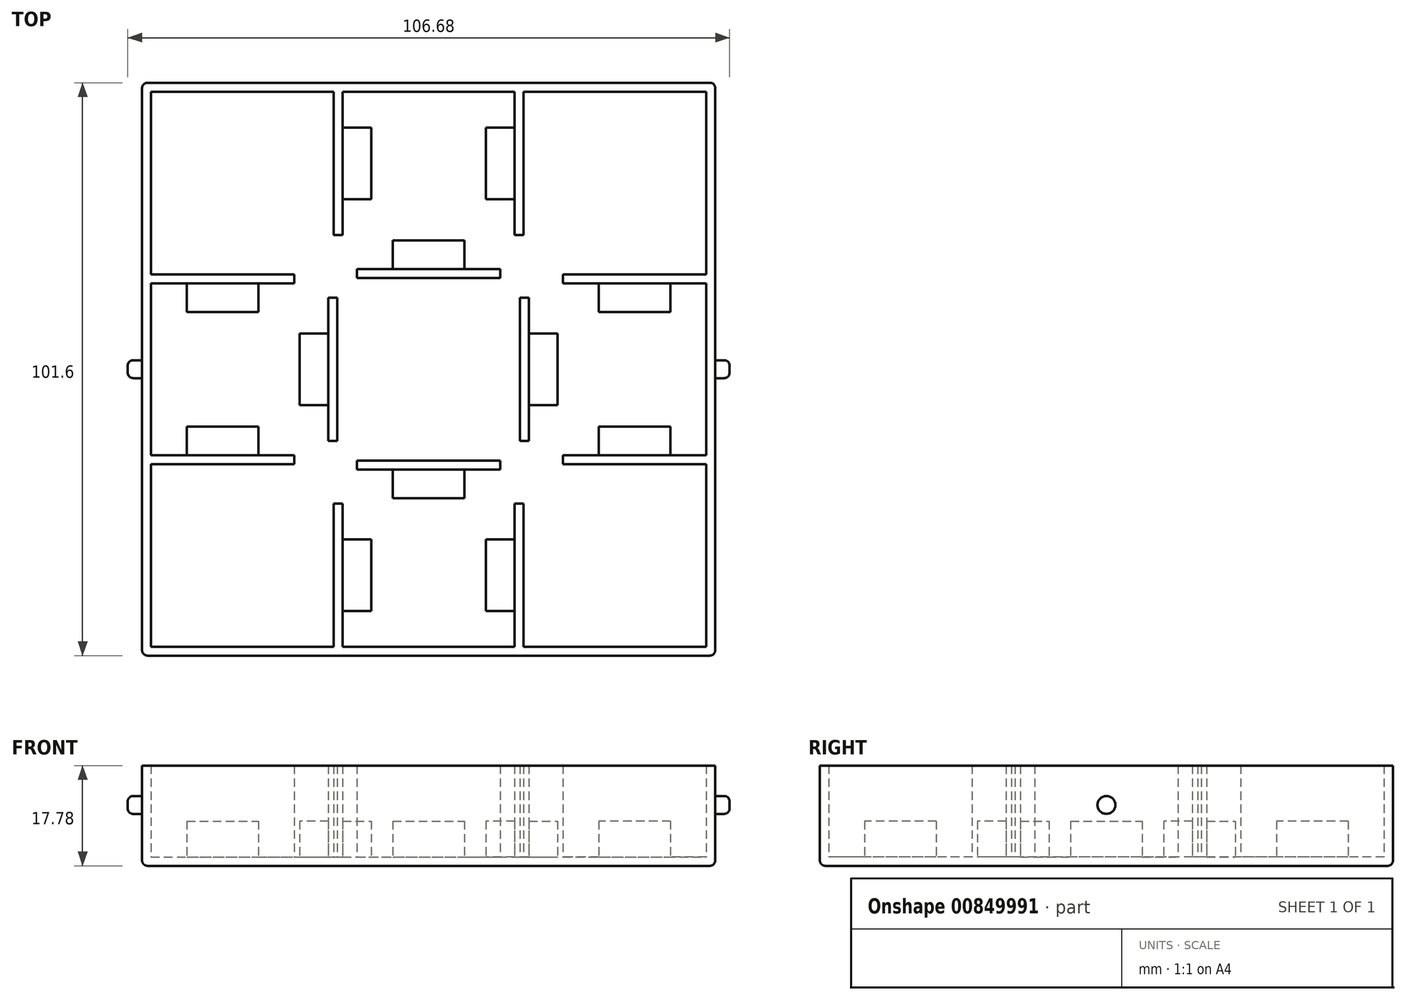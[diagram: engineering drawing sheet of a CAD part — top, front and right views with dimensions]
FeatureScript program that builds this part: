
annotation { "Feature Type Name" : "Feature", "Feature Type Description" : "" }
export const myFeature = defineFeature(function(context is Context, id is Id, definition is map)
    precondition{}
    {
        {
            var Q0;
            Q0=qCreatedBy(makeId("Top.planeOp"),FACE);
            var sketch = newSketch(context, id + "F0", { "sketchPlane" : qUnion([Q0])});
            skLineSegment(sketch, "E0.bottom", {"start": v(-50.8, 50.8) * mm, "end": v(50.8, 50.8) * mm});
            skLineSegment(sketch, "E0.top", {"start": v(-50.8, -50.8) * mm, "end": v(50.8, -50.8) * mm});
            skLineSegment(sketch, "E0.left", {"start": v(-50.8, 50.8) * mm, "end": v(-50.8, -50.8) * mm});
            skLineSegment(sketch, "E0.right", {"start": v(50.8, 50.8) * mm, "end": v(50.8, -50.8) * mm});
            skLineSegment(sketch, "E1", {"start": v(-50.8, 50.8) * mm, "end": v(50.8, -50.8) * mm, "construction": true});
            skSolve(sketch);
        }
        {
            var Q0;
            Q0 = qSketchRegion(id + "F0", true);
            extrude(context, id + "F1", {"entities" : qUnion([Q0]), "depth" : 1.59 * mm, "offsetDistance" : 25.4 * mm});
        }
        {
            var Q0;
            Q0=makeQuery(id+"F1.opExtrude","CAP_FACE",FACE,{"disambiguationData":[OSD([sQuery(id+"F0.wireOp",EDGE,"E0.bottom"),sQuery(id+"F0.wireOp",EDGE,"E0.top"),sQuery(id+"F0.wireOp",EDGE,"E0.left"),sQuery(id+"F0.wireOp",EDGE,"E0.right")])],"isStart":false});
            var sketch = newSketch(context, id + "F2", { "sketchPlane" : qUnion([Q0])});
            skLineSegment(sketch, "E2.bottom", {"start": v(-50.8, 50.8) * mm, "end": v(50.8, 50.8) * mm});
            skLineSegment(sketch, "E2.top", {"start": v(-50.8, -50.8) * mm, "end": v(50.8, -50.8) * mm});
            skLineSegment(sketch, "E2.left", {"start": v(-50.8, 50.8) * mm, "end": v(-50.8, -50.8) * mm});
            skLineSegment(sketch, "E2.right", {"start": v(50.8, 50.8) * mm, "end": v(50.8, -50.8) * mm});
            skLineSegment(sketch, "E3.0", {"start": v(49.21, 49.21) * mm, "end": v(49.21, -49.21) * mm});
            skLineSegment(sketch, "E3.1", {"start": v(-49.21, 49.21) * mm, "end": v(49.21, 49.21) * mm});
            skLineSegment(sketch, "E3.2", {"start": v(-49.21, 49.21) * mm, "end": v(-49.21, -49.21) * mm});
            skLineSegment(sketch, "E3.3", {"start": v(-49.21, -49.21) * mm, "end": v(49.21, -49.21) * mm});
            skSolve(sketch);
        }
        {
            var Q0;
            Q0 = qSketchRegion(id + "F2", true);
            extrude(context, id + "F3", {"entities" : qUnion([Q0]), "operationType" : NewBodyOperationType.ADD, "depth" : 16.2 * mm, "offsetDistance" : 25.4 * mm});
        }
        {
            var Q0;
            Q0=makeQuery(id+"F1.opExtrude","CAP_FACE",FACE,{"disambiguationData":[OSD([sQuery(id+"F0.wireOp",EDGE,"E0.bottom"),sQuery(id+"F0.wireOp",EDGE,"E0.top"),sQuery(id+"F0.wireOp",EDGE,"E0.left"),sQuery(id+"F0.wireOp",EDGE,"E0.right")])],"isStart":false});
            var sketch = newSketch(context, id + "F4", { "sketchPlane" : qUnion([Q0])});
            skLineSegment(sketch, "E4", {"start": v(-49.21, -16.83) * mm, "end": v(-23.81, -16.83) * mm});
            skLineSegment(sketch, "E5", {"start": v(-49.21, -15.24) * mm, "end": v(-23.81, -15.24) * mm});
            skLineSegment(sketch, "E6", {"start": v(-49.21, -15.24) * mm, "end": v(-49.21, -16.83) * mm});
            skLineSegment(sketch, "E7", {"start": v(49.21, -15.24) * mm, "end": v(49.21, -16.83) * mm});
            skLineSegment(sketch, "E8.bottom", {"start": v(-49.21, 16.83) * mm, "end": v(-23.81, 16.83) * mm});
            skLineSegment(sketch, "E8.top", {"start": v(-49.21, 15.24) * mm, "end": v(-23.81, 15.24) * mm});
            skLineSegment(sketch, "E8.left", {"start": v(-49.21, 16.83) * mm, "end": v(-49.21, 15.24) * mm});
            skLineSegment(sketch, "E8.right", {"start": v(49.21, 16.83) * mm, "end": v(49.21, 15.24) * mm});
            skLineSegment(sketch, "E9.bottom", {"start": v(15.24, 49.21) * mm, "end": v(16.83, 49.21) * mm});
            skLineSegment(sketch, "E9.left", {"start": v(15.24, 49.21) * mm, "end": v(15.24, 23.81) * mm});
            skLineSegment(sketch, "E9.right", {"start": v(16.83, 49.21) * mm, "end": v(16.83, 23.81) * mm});
            skLineSegment(sketch, "E10.bottom", {"start": v(-16.83, 49.21) * mm, "end": v(-15.24, 49.21) * mm});
            skLineSegment(sketch, "E10.left", {"start": v(-16.83, 49.21) * mm, "end": v(-16.83, 23.81) * mm});
            skLineSegment(sketch, "E10.right", {"start": v(-15.24, 49.21) * mm, "end": v(-15.24, 23.81) * mm});
            skLineSegment(sketch, "E11.top", {"start": v(-16.83, -49.21) * mm, "end": v(-15.24, -49.21) * mm});
            skLineSegment(sketch, "E11.left", {"start": v(-16.83, -23.81) * mm, "end": v(-16.83, -49.21) * mm});
            skLineSegment(sketch, "E11.right", {"start": v(-15.24, -23.81) * mm, "end": v(-15.24, -49.21) * mm});
            skLineSegment(sketch, "E12.top", {"start": v(15.24, -49.21) * mm, "end": v(16.83, -49.21) * mm});
            skLineSegment(sketch, "E12.left", {"start": v(15.24, -23.81) * mm, "end": v(15.24, -49.21) * mm});
            skLineSegment(sketch, "E12.right", {"start": v(16.83, -23.81) * mm, "end": v(16.83, -49.21) * mm});
            skLineSegment(sketch, "E13", {"start": v(-23.81, 16.83) * mm, "end": v(-23.81, 15.24) * mm});
            skLineSegment(sketch, "E14", {"start": v(-16.83, 23.81) * mm, "end": v(-15.24, 23.81) * mm});
            skLineSegment(sketch, "E15", {"start": v(15.24, 23.81) * mm, "end": v(16.83, 23.81) * mm});
            skLineSegment(sketch, "E16", {"start": v(23.81, 16.83) * mm, "end": v(23.81, 15.24) * mm});
            skLineSegment(sketch, "E17.trimOffspring", {"start": v(23.81, 16.83) * mm, "end": v(49.21, 16.83) * mm});
            skLineSegment(sketch, "E18.trimOffspring", {"start": v(23.81, 15.24) * mm, "end": v(49.21, 15.24) * mm});
            skLineSegment(sketch, "E19", {"start": v(-16.83, -23.81) * mm, "end": v(-15.24, -23.81) * mm});
            skLineSegment(sketch, "E20", {"start": v(-23.81, -15.24) * mm, "end": v(-23.81, -16.83) * mm});
            skLineSegment(sketch, "E21", {"start": v(49.21, -15.24) * mm, "end": v(23.81, -15.24) * mm});
            skLineSegment(sketch, "E22", {"start": v(23.81, -15.24) * mm, "end": v(23.81, -16.83) * mm});
            skLineSegment(sketch, "E23", {"start": v(23.81, -16.83) * mm, "end": v(49.21, -16.83) * mm});
            skLineSegment(sketch, "E24", {"start": v(15.24, -23.81) * mm, "end": v(16.83, -23.81) * mm});
            skLineSegment(sketch, "E25.bottom", {"start": v(-12.7, 16.2) * mm, "end": v(12.7, 16.2) * mm});
            skLineSegment(sketch, "E25.top", {"start": v(-12.7, -16.2) * mm, "end": v(12.7, -16.2) * mm});
            skLineSegment(sketch, "E25.left", {"start": v(-16.2, 12.7) * mm, "end": v(-16.2, -12.7) * mm});
            skLineSegment(sketch, "E25.right", {"start": v(16.2, 12.7) * mm, "end": v(16.2, -12.7) * mm});
            skLineSegment(sketch, "E26", {"start": v(-12.7, 16.2) * mm, "end": v(-12.7, 17.78) * mm});
            skLineSegment(sketch, "E27", {"start": v(-12.7, 17.78) * mm, "end": v(12.7, 17.78) * mm});
            skLineSegment(sketch, "E28", {"start": v(12.7, 17.78) * mm, "end": v(12.7, 16.2) * mm});
            skLineSegment(sketch, "E29", {"start": v(0, 17.78) * mm, "end": v(0, 16.2) * mm, "construction": true});
            skLineSegment(sketch, "E30", {"start": v(-12.7, -16.2) * mm, "end": v(-12.7, -17.78) * mm});
            skLineSegment(sketch, "E31", {"start": v(-12.7, -17.78) * mm, "end": v(12.7, -17.78) * mm});
            skLineSegment(sketch, "E32", {"start": v(12.7, -17.78) * mm, "end": v(12.7, -16.2) * mm});
            skLineSegment(sketch, "E33", {"start": v(0, -16.2) * mm, "end": v(0, -17.78) * mm, "construction": true});
            skLineSegment(sketch, "E34", {"start": v(16.2, 12.7) * mm, "end": v(17.78, 12.7) * mm});
            skLineSegment(sketch, "E35", {"start": v(17.78, 12.7) * mm, "end": v(17.78, -12.7) * mm});
            skLineSegment(sketch, "E36", {"start": v(17.78, -12.7) * mm, "end": v(16.2, -12.7) * mm});
            skLineSegment(sketch, "E37", {"start": v(16.2, 0) * mm, "end": v(17.78, 0) * mm, "construction": true});
            skLineSegment(sketch, "E38", {"start": v(-16.2, -12.7) * mm, "end": v(-17.78, -12.7) * mm});
            skLineSegment(sketch, "E39", {"start": v(-17.78, -12.7) * mm, "end": v(-17.78, 12.7) * mm});
            skLineSegment(sketch, "E40", {"start": v(-17.78, 12.7) * mm, "end": v(-16.2, 12.7) * mm});
            skLineSegment(sketch, "E41", {"start": v(-16.2, 0) * mm, "end": v(-17.78, 0) * mm, "construction": true});
            skLineSegment(sketch, "E42", {"start": v(0, 16.2) * mm, "end": v(0, 0) * mm, "construction": true});
            skLineSegment(sketch, "E43", {"start": v(0, 0) * mm, "end": v(0, -16.2) * mm, "construction": true});
            skLineSegment(sketch, "E44", {"start": v(-16.2, 0) * mm, "end": v(0, 0) * mm, "construction": true});
            skLineSegment(sketch, "E45", {"start": v(16.2, 0) * mm, "end": v(0, 0) * mm, "construction": true});
            skLineSegment(sketch, "E46", {"start": v(0, 49.21) * mm, "end": v(0, 17.78) * mm, "construction": true});
            skLineSegment(sketch, "E47", {"start": v(0, -17.78) * mm, "end": v(0, -49.21) * mm, "construction": true});
            skLineSegment(sketch, "E48", {"start": v(-49.21, 0) * mm, "end": v(-17.78, 0) * mm, "construction": true});
            skLineSegment(sketch, "E49", {"start": v(17.78, 0) * mm, "end": v(49.21, 0) * mm, "construction": true});
            skSolve(sketch);
        }
        {
            var Q0;
            Q0 = qSketchRegion(id + "F4", true);
            var Q1;
            Q1=makeQuery(id+"F3.opExtrude","CAP_FACE",FACE,{"disambiguationData":[OSD([sQuery(id+"F2.wireOp",EDGE,"E2.bottom"),sQuery(id+"F2.wireOp",EDGE,"E2.top"),sQuery(id+"F2.wireOp",EDGE,"E2.left"),sQuery(id+"F2.wireOp",EDGE,"E2.right"),sQuery(id+"F2.wireOp",EDGE,"E3.0"),sQuery(id+"F2.wireOp",EDGE,"E3.1"),sQuery(id+"F2.wireOp",EDGE,"E3.2"),sQuery(id+"F2.wireOp",EDGE,"E3.3")])],"isStart":false});
            extrude(context, id + "F5", {"entities" : qUnion([Q0]), "operationType" : NewBodyOperationType.ADD, "endBound" : BoundingType.UP_TO_SURFACE, "depth" : 25.4 * mm, "endBoundEntityFace" : qUnion([Q1]), "offsetDistance" : 25.4 * mm});
        }
        {
            var Q0;
            Q0=makeQuery(id+"F1.opExtrude","CAP_FACE",FACE,{"disambiguationData":[OSD([sQuery(id+"F0.wireOp",EDGE,"E0.bottom"),sQuery(id+"F0.wireOp",EDGE,"E0.top"),sQuery(id+"F0.wireOp",EDGE,"E0.left"),sQuery(id+"F0.wireOp",EDGE,"E0.right")])],"isStart":false});
            var sketch = newSketch(context, id + "F6", { "sketchPlane" : qUnion([Q0])});
            skLineSegment(sketch, "E50.bottom", {"start": v(-42.86, 15.24) * mm, "end": v(-30.16, 15.24) * mm});
            skLineSegment(sketch, "E50.top", {"start": v(-42.86, 10.16) * mm, "end": v(-30.16, 10.16) * mm});
            skLineSegment(sketch, "E50.left", {"start": v(-42.86, 15.24) * mm, "end": v(-42.86, 10.16) * mm});
            skLineSegment(sketch, "E50.right", {"start": v(-30.16, 15.24) * mm, "end": v(-30.16, 10.16) * mm});
            skLineSegment(sketch, "E51.bottom", {"start": v(-42.86, -15.24) * mm, "end": v(-30.16, -15.24) * mm});
            skLineSegment(sketch, "E51.top", {"start": v(-42.86, -10.16) * mm, "end": v(-30.16, -10.16) * mm});
            skLineSegment(sketch, "E51.left", {"start": v(-42.86, -15.24) * mm, "end": v(-42.86, -10.16) * mm});
            skLineSegment(sketch, "E51.right", {"start": v(-30.16, -15.24) * mm, "end": v(-30.16, -10.16) * mm});
            skLineSegment(sketch, "E52.bottom", {"start": v(-15.24, 42.86) * mm, "end": v(-10.16, 42.86) * mm});
            skLineSegment(sketch, "E52.top", {"start": v(-15.24, 30.16) * mm, "end": v(-10.16, 30.16) * mm});
            skLineSegment(sketch, "E52.left", {"start": v(-15.24, 42.86) * mm, "end": v(-15.24, 30.16) * mm});
            skLineSegment(sketch, "E52.right", {"start": v(-10.16, 42.86) * mm, "end": v(-10.16, 30.16) * mm});
            skLineSegment(sketch, "E53.bottom", {"start": v(15.24, 42.86) * mm, "end": v(10.16, 42.86) * mm});
            skLineSegment(sketch, "E53.top", {"start": v(15.24, 30.16) * mm, "end": v(10.16, 30.16) * mm});
            skLineSegment(sketch, "E53.left", {"start": v(15.24, 42.86) * mm, "end": v(15.24, 30.16) * mm});
            skLineSegment(sketch, "E53.right", {"start": v(10.16, 42.86) * mm, "end": v(10.16, 30.16) * mm});
            skLineSegment(sketch, "E54.bottom", {"start": v(30.16, 15.24) * mm, "end": v(42.86, 15.24) * mm});
            skLineSegment(sketch, "E54.top", {"start": v(30.16, 10.16) * mm, "end": v(42.86, 10.16) * mm});
            skLineSegment(sketch, "E54.left", {"start": v(30.16, 15.24) * mm, "end": v(30.16, 10.16) * mm});
            skLineSegment(sketch, "E54.right", {"start": v(42.86, 15.24) * mm, "end": v(42.86, 10.16) * mm});
            skLineSegment(sketch, "E55.bottom", {"start": v(30.16, -15.24) * mm, "end": v(42.86, -15.24) * mm});
            skLineSegment(sketch, "E55.top", {"start": v(30.16, -10.16) * mm, "end": v(42.86, -10.16) * mm});
            skLineSegment(sketch, "E55.left", {"start": v(30.16, -15.24) * mm, "end": v(30.16, -10.16) * mm});
            skLineSegment(sketch, "E55.right", {"start": v(42.86, -15.24) * mm, "end": v(42.86, -10.16) * mm});
            skLineSegment(sketch, "E56.bottom", {"start": v(15.24, -30.16) * mm, "end": v(10.16, -30.16) * mm});
            skLineSegment(sketch, "E56.top", {"start": v(15.24, -42.86) * mm, "end": v(10.16, -42.86) * mm});
            skLineSegment(sketch, "E56.left", {"start": v(15.24, -30.16) * mm, "end": v(15.24, -42.86) * mm});
            skLineSegment(sketch, "E56.right", {"start": v(10.16, -30.16) * mm, "end": v(10.16, -42.86) * mm});
            skLineSegment(sketch, "E57.bottom", {"start": v(-15.24, -30.16) * mm, "end": v(-10.16, -30.16) * mm});
            skLineSegment(sketch, "E57.top", {"start": v(-15.24, -42.86) * mm, "end": v(-10.16, -42.86) * mm});
            skLineSegment(sketch, "E57.left", {"start": v(-15.24, -30.16) * mm, "end": v(-15.24, -42.86) * mm});
            skLineSegment(sketch, "E57.right", {"start": v(-10.16, -30.16) * mm, "end": v(-10.16, -42.86) * mm});
            skLineSegment(sketch, "E58.bottom", {"start": v(-6.35, -17.78) * mm, "end": v(6.35, -17.78) * mm});
            skLineSegment(sketch, "E58.top", {"start": v(-6.35, -22.86) * mm, "end": v(6.35, -22.86) * mm});
            skLineSegment(sketch, "E58.left", {"start": v(-6.35, -17.78) * mm, "end": v(-6.35, -22.86) * mm});
            skLineSegment(sketch, "E58.right", {"start": v(6.35, -17.78) * mm, "end": v(6.35, -22.86) * mm});
            skLineSegment(sketch, "E59.bottom", {"start": v(17.78, 6.35) * mm, "end": v(22.86, 6.35) * mm});
            skLineSegment(sketch, "E59.top", {"start": v(17.78, -6.35) * mm, "end": v(22.86, -6.35) * mm});
            skLineSegment(sketch, "E59.left", {"start": v(17.78, 6.35) * mm, "end": v(17.78, -6.35) * mm});
            skLineSegment(sketch, "E59.right", {"start": v(22.86, 6.35) * mm, "end": v(22.86, -6.35) * mm});
            skLineSegment(sketch, "E60.bottom", {"start": v(-17.78, 6.35) * mm, "end": v(-22.86, 6.35) * mm});
            skLineSegment(sketch, "E60.left", {"start": v(-17.78, 6.35) * mm, "end": v(-17.78, -6.35) * mm});
            skLineSegment(sketch, "E61.bottom", {"start": v(-6.35, 17.78) * mm, "end": v(6.35, 17.78) * mm});
            skLineSegment(sketch, "E61.top", {"start": v(-6.35, 22.86) * mm, "end": v(6.35, 22.86) * mm});
            skLineSegment(sketch, "E61.left", {"start": v(-6.35, 17.78) * mm, "end": v(-6.35, 22.86) * mm});
            skLineSegment(sketch, "E61.right", {"start": v(6.35, 17.78) * mm, "end": v(6.35, 22.86) * mm});
            skLineSegment(sketch, "E62", {"start": v(-22.86, 6.35) * mm, "end": v(-22.86, -6.35) * mm});
            skLineSegment(sketch, "E63", {"start": v(-22.86, -6.35) * mm, "end": v(-17.78, -6.35) * mm});
            skSolve(sketch);
        }
        {
            var Q0;
            Q0 = qSketchRegion(id + "F6", true);
            extrude(context, id + "F7", {"entities" : qUnion([Q0]), "operationType" : NewBodyOperationType.ADD, "depth" : 6.35 * mm, "offsetDistance" : 25.4 * mm});
        }
        {
            var Q0;
            Q0=makeQuery(id+"F3.boolean.opBoolean","MERGE",FACE,{"derivedFrom":[makeQuery(id+"F1.opExtrude","SWEPT_FACE",FACE,{"disambiguationData":[OSD([sQuery(id+"F0.wireOp",EDGE,"E0.right")])]}),makeQuery(id+"F3.opExtrude","SWEPT_FACE",FACE,{"disambiguationData":[OSD([sQuery(id+"F2.wireOp",EDGE,"E2.right")])]})]});
            var sketch = newSketch(context, id + "F8", { "sketchPlane" : qUnion([Q0])});
            skCircle(sketch, "E64", {"center": v(0, 10.8) * mm, "radius": 1.59 * mm});
            skSolve(sketch);
        }
        {
            var Q0;
            Q0 = qSketchRegion(id + "F8", true);
            extrude(context, id + "F9", {"entities" : qUnion([Q0]), "operationType" : NewBodyOperationType.ADD, "depth" : 2.54 * mm, "offsetDistance" : 25.4 * mm});
        }
        {
            var Q0;
            Q0=makeQuery(id+"F1.opExtrude","SWEPT_BODY",BODY,{"disambiguationData":[OSD([sQuery(id+"F0.wireOp",EDGE,"E0.bottom"),sQuery(id+"F0.wireOp",EDGE,"E0.top"),sQuery(id+"F0.wireOp",EDGE,"E0.left"),sQuery(id+"F0.wireOp",EDGE,"E0.right")])]});
            var Q1;
            Q1=qCreatedBy(makeId("Right.planeOp"),FACE);
            mirror(context, id + "F10", {"operationType" : NewBodyOperationType.ADD, "entities" : qUnion([Q0]), "mirrorPlane" : qUnion([Q1])});
        }
        {
            var Q0;
            Q0=makeQuery(id+"F10.opPattern","COPY",EDGE,{"derivedFrom":makeQuery(id+"F9.opExtrude","CAP_EDGE",EDGE,{"disambiguationData":[OSD([sQuery(id+"F8.wireOp",EDGE,"E64")])],"isStart":false}),"instanceName":"1"});
            var Q1;
            Q1=makeQuery(id+"F3.boolean.opBoolean","MERGE",EDGE,{"derivedFrom":[makeQuery(id+"F1.opExtrude","SWEPT_EDGE",EDGE,{"disambiguationData":[OSD([sQuery(id+"F0.wireOp",EDGE,"E0.top"),sQuery(id+"F0.wireOp",EDGE,"E0.left")])]}),makeQuery(id+"F3.opExtrude","SWEPT_EDGE",EDGE,{"disambiguationData":[OSD([sQuery(id+"F2.wireOp",EDGE,"E2.top"),sQuery(id+"F2.wireOp",EDGE,"E2.left")])]})]});
            var Q2;
            Q2=makeQuery(id+"F1.opExtrude","CAP_EDGE",EDGE,{"disambiguationData":[OSD([sQuery(id+"F0.wireOp",EDGE,"E0.top")])],"isStart":true});
            var Q3;
            Q3=makeQuery(id+"F3.boolean.opBoolean","MERGE",EDGE,{"derivedFrom":[makeQuery(id+"F1.opExtrude","SWEPT_EDGE",EDGE,{"disambiguationData":[OSD([sQuery(id+"F0.wireOp",EDGE,"E0.top"),sQuery(id+"F0.wireOp",EDGE,"E0.right")])]}),makeQuery(id+"F3.opExtrude","SWEPT_EDGE",EDGE,{"disambiguationData":[OSD([sQuery(id+"F2.wireOp",EDGE,"E2.top"),sQuery(id+"F2.wireOp",EDGE,"E2.right")])]})]});
            var Q4;
            Q4=makeQuery(id+"F9.opExtrude","CAP_EDGE",EDGE,{"disambiguationData":[OSD([sQuery(id+"F8.wireOp",EDGE,"E64")])],"isStart":false});
            var Q5;
            Q5=makeQuery(id+"F1.opExtrude","CAP_EDGE",EDGE,{"disambiguationData":[OSD([sQuery(id+"F0.wireOp",EDGE,"E0.right")])],"isStart":true});
            var Q6;
            Q6=makeQuery(id+"F1.opExtrude","CAP_EDGE",EDGE,{"disambiguationData":[OSD([sQuery(id+"F0.wireOp",EDGE,"E0.bottom")])],"isStart":true});
            var Q7;
            Q7=makeQuery(id+"F3.boolean.opBoolean","MERGE",EDGE,{"derivedFrom":[makeQuery(id+"F1.opExtrude","SWEPT_EDGE",EDGE,{"disambiguationData":[OSD([sQuery(id+"F0.wireOp",EDGE,"E0.bottom"),sQuery(id+"F0.wireOp",EDGE,"E0.right")])]}),makeQuery(id+"F3.opExtrude","SWEPT_EDGE",EDGE,{"disambiguationData":[OSD([sQuery(id+"F2.wireOp",EDGE,"E2.bottom"),sQuery(id+"F2.wireOp",EDGE,"E2.right")])]})]});
            var Q8;
            Q8=makeQuery(id+"F1.opExtrude","CAP_EDGE",EDGE,{"disambiguationData":[OSD([sQuery(id+"F0.wireOp",EDGE,"E0.left")])],"isStart":true});
            var Q9;
            Q9=makeQuery(id+"F3.boolean.opBoolean","MERGE",EDGE,{"derivedFrom":[makeQuery(id+"F1.opExtrude","SWEPT_EDGE",EDGE,{"disambiguationData":[OSD([sQuery(id+"F0.wireOp",EDGE,"E0.bottom"),sQuery(id+"F0.wireOp",EDGE,"E0.left")])]}),makeQuery(id+"F3.opExtrude","SWEPT_EDGE",EDGE,{"disambiguationData":[OSD([sQuery(id+"F2.wireOp",EDGE,"E2.bottom"),sQuery(id+"F2.wireOp",EDGE,"E2.left")])]})]});
            fillet(context, id + "F11", {"entities" : qUnion([Q0, Q1, Q2, Q3, Q4, Q5, Q6, Q7, Q8, Q9]), "radius" : 0.95 * mm, "tangentPropagation" : true, "allowEdgeOverflow" : false});
        }
    });
